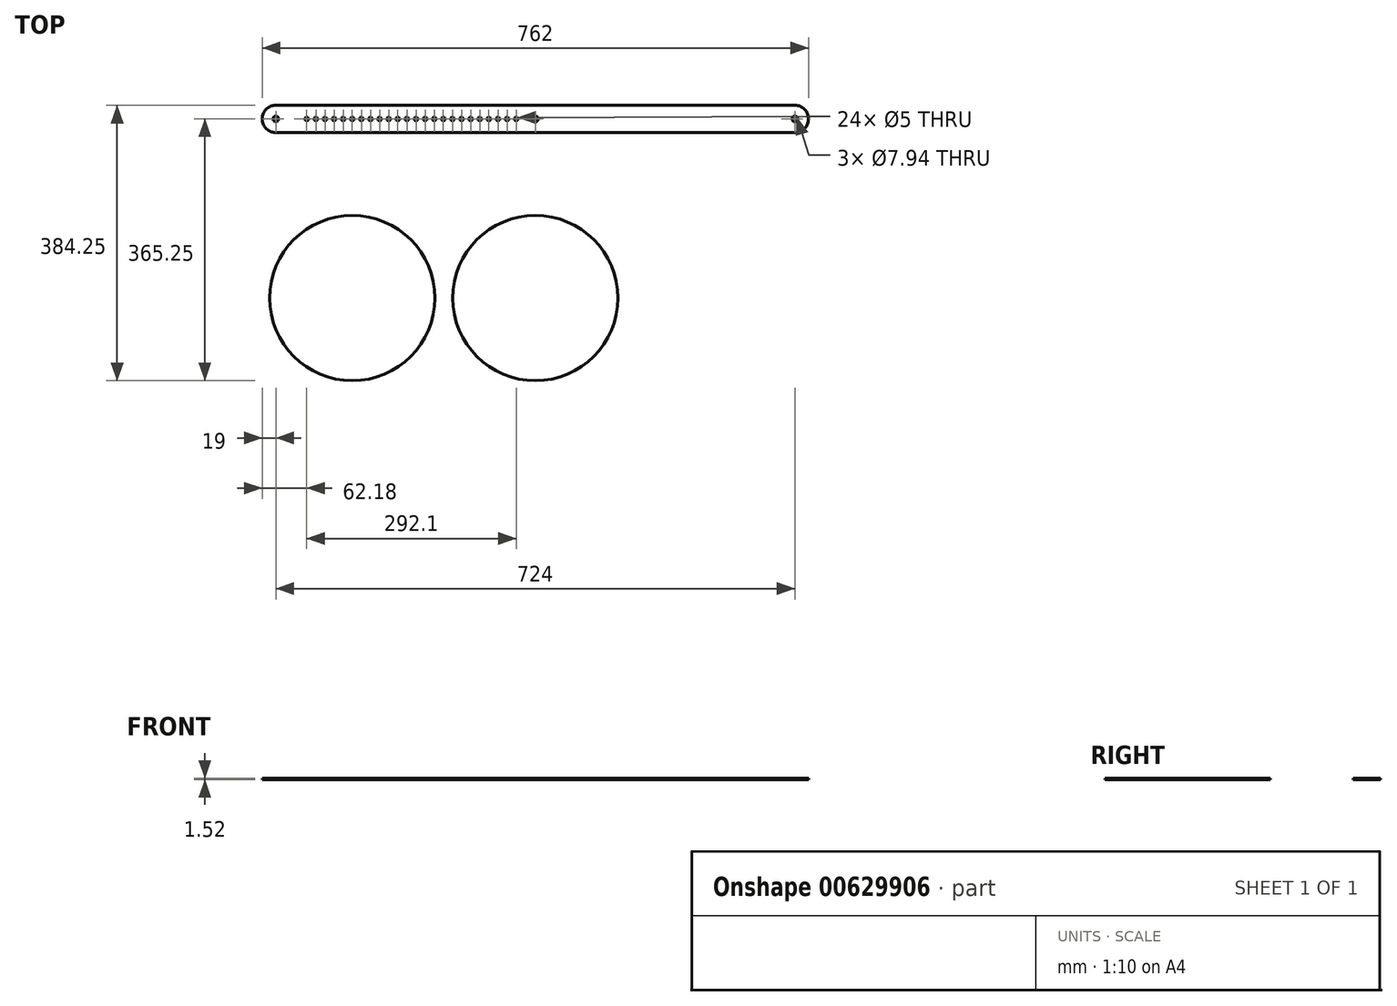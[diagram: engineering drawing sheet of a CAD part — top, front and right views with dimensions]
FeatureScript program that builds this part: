
annotation { "Feature Type Name" : "Feature", "Feature Type Description" : "" }
export const myFeature = defineFeature(function(context is Context, id is Id, definition is map)
    precondition{}
    {
        {
            var Q0;
            Q0=qCreatedBy(makeId("Top.planeOp"),FACE);
            var sketch = newSketch(context, id + "F0", { "sketchPlane" : qUnion([Q0])});
            skLineSegment(sketch, "E0.bottom", {"start": v(19, 0) * mm, "end": v(743, 0) * mm});
            skLineSegment(sketch, "E0.top", {"start": v(19, -38) * mm, "end": v(743, -38) * mm});
            skLineSegment(sketch, "E1", {"start": v(0, -19) * mm, "end": v(762, -19) * mm, "construction": true});
            skCircle(sketch, "E2", {"center": v(62.18, -19) * mm, "radius": 2.5 * mm});
            skCircle(sketch, "E3", {"center": v(74.88, -19) * mm, "radius": 2.5 * mm});
            skLineSegment(sketch, "E4", {"start": v(381, 0) * mm, "end": v(381, -38) * mm, "construction": true});
            skLineSegment(sketch, "E5", {"start": v(743, 0) * mm, "end": v(743, -38) * mm, "construction": true});
            skCircle(sketch, "E6", {"center": v(743, -19) * mm, "radius": 3.97 * mm});
            skCircle(sketch, "E7.MirrorC", {"center": v(19, -19) * mm, "radius": 3.97 * mm});
            skCircle(sketch, "E8", {"center": v(87.58, -19) * mm, "radius": 2.5 * mm});
            skCircle(sketch, "E9", {"center": v(100.28, -19) * mm, "radius": 2.5 * mm});
            skCircle(sketch, "E10", {"center": v(112.98, -19) * mm, "radius": 2.5 * mm});
            skCircle(sketch, "E11", {"center": v(125.68, -19) * mm, "radius": 2.5 * mm});
            skCircle(sketch, "E12", {"center": v(138.38, -19) * mm, "radius": 2.5 * mm});
            skCircle(sketch, "E13", {"center": v(151.08, -19) * mm, "radius": 2.5 * mm});
            skCircle(sketch, "E14", {"center": v(163.78, -19) * mm, "radius": 2.5 * mm});
            skCircle(sketch, "E15", {"center": v(176.48, -19) * mm, "radius": 2.5 * mm});
            skCircle(sketch, "E16", {"center": v(189.18, -19) * mm, "radius": 2.5 * mm});
            skCircle(sketch, "E17", {"center": v(201.88, -19) * mm, "radius": 2.5 * mm});
            skCircle(sketch, "E18", {"center": v(214.58, -19) * mm, "radius": 2.5 * mm});
            skCircle(sketch, "E19", {"center": v(227.28, -19) * mm, "radius": 2.5 * mm});
            skCircle(sketch, "E20", {"center": v(239.98, -19) * mm, "radius": 2.5 * mm});
            skCircle(sketch, "E21", {"center": v(252.68, -19) * mm, "radius": 2.5 * mm});
            skCircle(sketch, "E22", {"center": v(265.38, -19) * mm, "radius": 2.5 * mm});
            skCircle(sketch, "E23", {"center": v(278.08, -19) * mm, "radius": 2.5 * mm});
            skCircle(sketch, "E24", {"center": v(290.78, -19) * mm, "radius": 2.5 * mm});
            skCircle(sketch, "E25", {"center": v(303.48, -19) * mm, "radius": 2.5 * mm});
            skCircle(sketch, "E26", {"center": v(316.18, -19) * mm, "radius": 2.5 * mm});
            skCircle(sketch, "E27", {"center": v(328.88, -19) * mm, "radius": 2.5 * mm});
            skCircle(sketch, "E28", {"center": v(341.58, -19) * mm, "radius": 2.5 * mm});
            skCircle(sketch, "E29", {"center": v(354.28, -19) * mm, "radius": 2.5 * mm});
            skCircle(sketch, "E30", {"center": v(381, -19) * mm, "radius": 3.97 * mm});
            skArc(sketch, "E31", {"start": v(743, -38) * mm, "mid": v(762, -19) * mm, "end": v(743, 0) * mm});
            skArc(sketch, "E32", {"start": v(19, 0) * mm, "mid": v(0, -19) * mm, "end": v(19, -38) * mm});
            skLineSegment(sketch, "E33", {"start": v(0, 0) * mm, "end": v(19, 0) * mm, "construction": true});
            skLineSegment(sketch, "E34", {"start": v(0, 0) * mm, "end": v(0, -19) * mm, "construction": true});
            skPoint(sketch, "E35.orphan", {"position": v(0, -38) * mm});
            skLineSegment(sketch, "E36", {"start": v(0, -19) * mm, "end": v(0, -38) * mm, "construction": true});
            skLineSegment(sketch, "E37", {"start": v(0, -38) * mm, "end": v(19, -38) * mm, "construction": true});
            skPoint(sketch, "E38.orphan", {"position": v(762, 0) * mm});
            skPoint(sketch, "E39.orphan", {"position": v(762, -38) * mm});
            skLineSegment(sketch, "E40", {"start": v(743, 0) * mm, "end": v(762, 0) * mm, "construction": true});
            skLineSegment(sketch, "E41", {"start": v(762, 0) * mm, "end": v(762, -19) * mm, "construction": true});
            skLineSegment(sketch, "E42", {"start": v(762, -19) * mm, "end": v(762, -38) * mm, "construction": true});
            skLineSegment(sketch, "E43", {"start": v(762, -38) * mm, "end": v(743, -38) * mm, "construction": true});
            skLineSegment(sketch, "E44", {"start": v(125.68, -19) * mm, "end": v(125.68, -269) * mm, "construction": true});
            skCircle(sketch, "E45", {"center": v(125.68, -269) * mm, "radius": 115.25 * mm});
            skCircle(sketch, "E46", {"center": v(381, -269) * mm, "radius": 115.25 * mm});
            skLineSegment(sketch, "E47", {"start": v(381, -19) * mm, "end": v(381, -269) * mm, "construction": true});
            skSolve(sketch);
        }
        {
            var Q0;
            Q0=makeQuery(id+"F0.imprint","IMPRINT",FACE,{"disambiguationData":[TD([[makeQuery(id+"F0.imprint","IMPRINT",EDGE,{"derivedFrom":sQuery(id+"F0.wireOp",EDGE,"E0.bottom")}),-1.0]])]});
            var Q1;
            Q1=makeQuery(id+"F0.imprint","IMPRINT",FACE,{"disambiguationData":[TD([[makeQuery(id+"F0.imprint","IMPRINT",EDGE,{"derivedFrom":sQuery(id+"F0.wireOp",EDGE,"E46")}),1.0]])]});
            var Q2;
            Q2=makeQuery(id+"F0.imprint","IMPRINT",FACE,{"disambiguationData":[TD([[makeQuery(id+"F0.imprint","IMPRINT",EDGE,{"derivedFrom":sQuery(id+"F0.wireOp",EDGE,"E45")}),1.0]])]});
            extrude(context, id + "F1", {"entities" : qUnion([Q0, Q1, Q2]), "depth" : 1.52 * mm, "offsetDistance" : 25.4 * mm});
        }
    });
